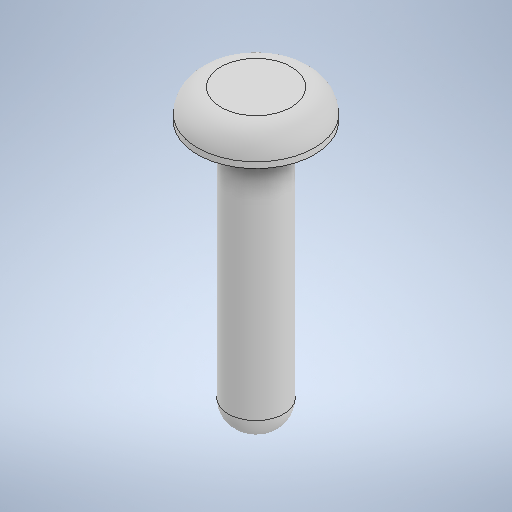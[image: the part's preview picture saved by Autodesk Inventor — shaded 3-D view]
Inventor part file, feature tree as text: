
AUTODESK INVENTOR PART (.ipt)
format: ipt  version: 2025.2 (Build 292293000, 293)  size: 260,096 bytes
history: native  units: mm
features: extrude x2, fillet x2, sketch x2
ambient origin geometry x8: Origin, YZ Plane, XZ Plane, XY Plane, X Axis, Y Axis, Z Axis, Center Point
bodies: Solid1 (feature_tree)
feature tree (6):
  extrude  "Extrusion1"  Depth=45.0mm TaperAngle=0.0deg
  extrude  "Extrusion2"  Depth=5.0mm TaperAngle=0.0deg
  fillet  "Fillet1"  Radius=4.0mm
  fillet  "Fillet2"  Radius=4.0mm
  sketch  "Sketch1"  dims[d0=9.5mm d1=45.0mm d2=0.0mm]
  sketch  "Sketch2"  dims[d3=20.0mm d4=5.0mm d5=0.0mm d6=4.0mm d7=4.0mm]
